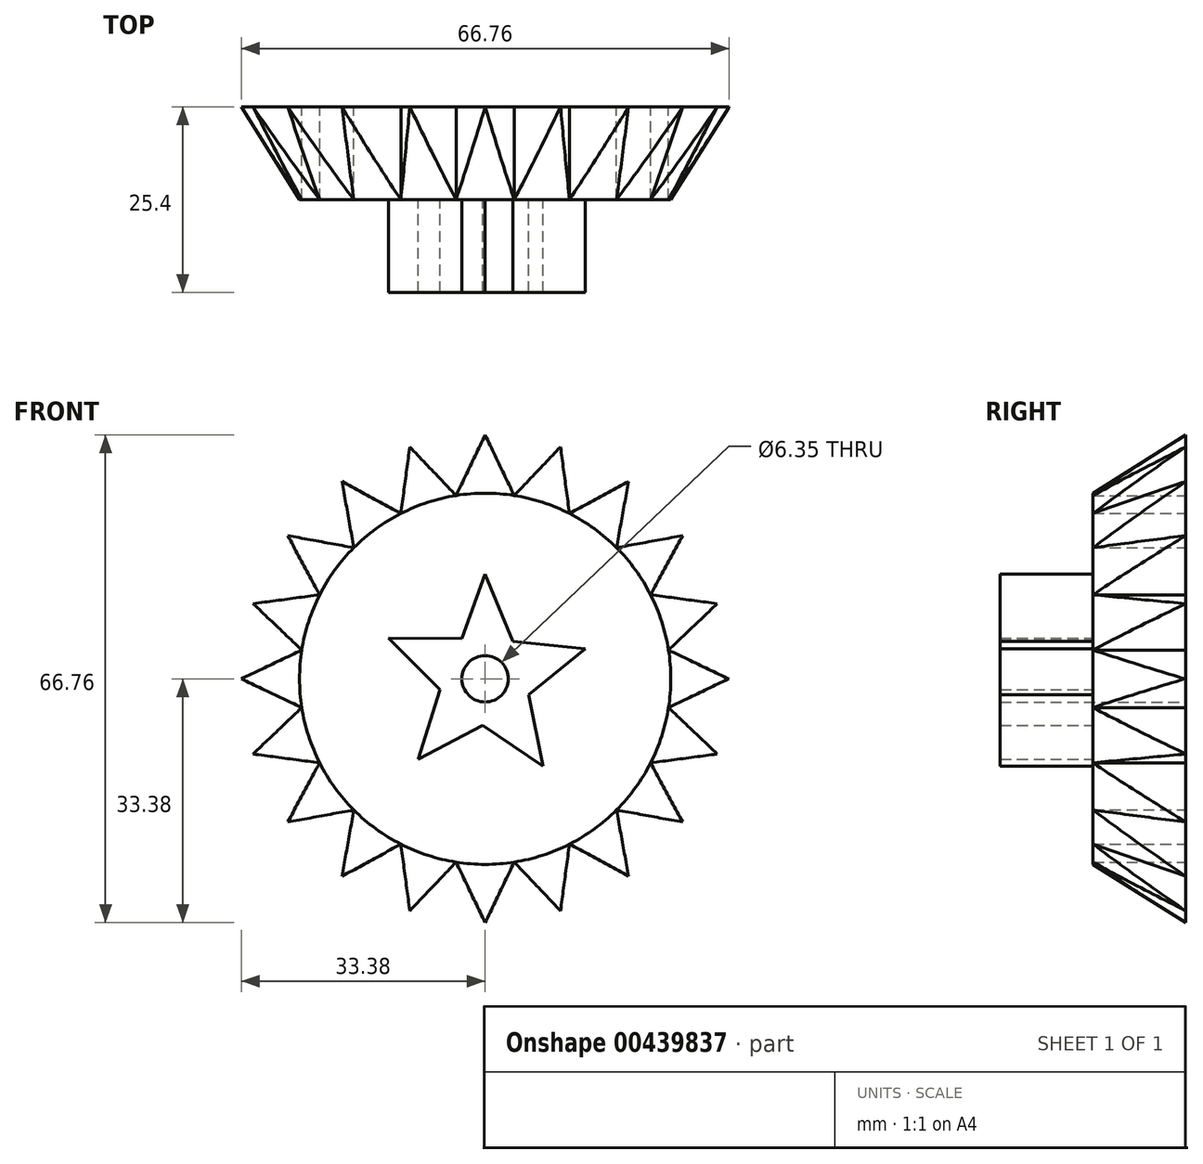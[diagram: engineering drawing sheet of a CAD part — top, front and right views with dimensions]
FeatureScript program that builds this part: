
annotation { "Feature Type Name" : "Feature", "Feature Type Description" : "" }
export const myFeature = defineFeature(function(context is Context, id is Id, definition is map)
    precondition{}
    {
        {
            var Q0;
            Q0=qCreatedBy(makeId("Front.planeOp"),FACE);
            var sketch = newSketch(context, id + "F0", { "sketchPlane" : qUnion([Q0])});
            skCircle(sketch, "E0", {"center": v(0, 0) * mm, "radius": 25.4 * mm});
            skPoint(sketch, "E1", {"position": v(0, 25.4) * mm});
            skPoint(sketch, "E2", {"position": v(3.98, 25.09) * mm});
            skPoint(sketch, "E3", {"position": v(7.86, 24.15) * mm});
            skPoint(sketch, "E4", {"position": v(11.54, 22.63) * mm});
            skPoint(sketch, "E5", {"position": v(14.94, 20.54) * mm});
            skPoint(sketch, "E6", {"position": v(17.98, 17.95) * mm});
            skPoint(sketch, "E7", {"position": v(20.56, 14.9) * mm});
            skPoint(sketch, "E8", {"position": v(22.64, 11.5) * mm});
            skPoint(sketch, "E9", {"position": v(24.17, 7.82) * mm});
            skPoint(sketch, "E10", {"position": v(25.1, 3.94) * mm});
            skPoint(sketch, "E11", {"position": v(25.4, -0.04) * mm});
            skPoint(sketch, "E12", {"position": v(25.08, -4.02) * mm});
            skPoint(sketch, "E13", {"position": v(24.14, -7.9) * mm});
            skPoint(sketch, "E14", {"position": v(22.6, -11.58) * mm});
            skPoint(sketch, "E15", {"position": v(20.52, -14.98) * mm});
            skPoint(sketch, "E16", {"position": v(17.92, -18) * mm});
            skPoint(sketch, "E17", {"position": v(14.88, -20.59) * mm});
            skPoint(sketch, "E18", {"position": v(11.47, -22.66) * mm});
            skPoint(sketch, "E19", {"position": v(7.78, -24.18) * mm});
            skPoint(sketch, "E20", {"position": v(3.9, -25.1) * mm});
            skPoint(sketch, "E21", {"position": v(-0.08, -25.4) * mm});
            skPoint(sketch, "E22.MirrorP", {"position": v(-3.98, 25.09) * mm});
            skPoint(sketch, "E23.MirrorP", {"position": v(-7.86, 24.15) * mm});
            skPoint(sketch, "E24.MirrorP", {"position": v(-11.54, 22.63) * mm});
            skPoint(sketch, "E25.MirrorP", {"position": v(-14.94, 20.54) * mm});
            skPoint(sketch, "E26.MirrorP", {"position": v(-17.98, 17.95) * mm});
            skPoint(sketch, "E27.MirrorP", {"position": v(-20.56, 14.9) * mm});
            skPoint(sketch, "E28.MirrorP", {"position": v(-22.64, 11.5) * mm});
            skPoint(sketch, "E29.MirrorP", {"position": v(-24.17, 7.82) * mm});
            skPoint(sketch, "E30.MirrorP", {"position": v(-25.1, 3.94) * mm});
            skPoint(sketch, "E31.MirrorP", {"position": v(-25.4, -0.04) * mm});
            skPoint(sketch, "E32.MirrorP", {"position": v(-25.08, -4.02) * mm});
            skPoint(sketch, "E33.MirrorP", {"position": v(-24.14, -7.9) * mm});
            skPoint(sketch, "E34.MirrorP", {"position": v(-22.6, -11.58) * mm});
            skPoint(sketch, "E35.MirrorP", {"position": v(-20.52, -14.98) * mm});
            skPoint(sketch, "E36.MirrorP", {"position": v(-17.92, -18) * mm});
            skPoint(sketch, "E37.MirrorP", {"position": v(-14.88, -20.59) * mm});
            skPoint(sketch, "E38.MirrorP", {"position": v(-11.47, -22.66) * mm});
            skPoint(sketch, "E39.MirrorP", {"position": v(-7.78, -24.18) * mm});
            skPoint(sketch, "E40.MirrorP", {"position": v(-3.9, -25.1) * mm});
            skLineSegment(sketch, "E41", {"start": v(0, 25.4) * mm, "end": v(-0.08, -25.4) * mm});
            skLineSegment(sketch, "E42", {"start": v(7.86, 24.15) * mm, "end": v(-7.78, -24.18) * mm});
            skLineSegment(sketch, "E43", {"start": v(14.94, 20.54) * mm, "end": v(-14.88, -20.59) * mm});
            skLineSegment(sketch, "E44", {"start": v(20.56, 14.9) * mm, "end": v(-20.52, -14.98) * mm});
            skLineSegment(sketch, "E45", {"start": v(24.17, 7.82) * mm, "end": v(-24.14, -7.9) * mm});
            skLineSegment(sketch, "E46", {"start": v(-25.4, -0.04) * mm, "end": v(25.4, -0.04) * mm});
            skLineSegment(sketch, "E47", {"start": v(24.14, -7.9) * mm, "end": v(-24.17, 7.82) * mm});
            skLineSegment(sketch, "E48", {"start": v(-20.56, 14.9) * mm, "end": v(20.52, -14.98) * mm});
            skLineSegment(sketch, "E49", {"start": v(14.88, -20.59) * mm, "end": v(-14.94, 20.54) * mm});
            skLineSegment(sketch, "E50", {"start": v(-7.86, 24.15) * mm, "end": v(7.78, -24.18) * mm});
            skLineSegment(sketch, "E51", {"start": v(0, 25.4) * mm, "end": v(0, 33.38) * mm});
            skLineSegment(sketch, "E52", {"start": v(0, 33.38) * mm, "end": v(3.98, 25.09) * mm});
            skLineSegment(sketch, "E53", {"start": v(7.86, 24.15) * mm, "end": v(10.31, 31.75) * mm});
            skLineSegment(sketch, "E54", {"start": v(-7.86, 24.15) * mm, "end": v(-10.31, 31.75) * mm});
            skLineSegment(sketch, "E55", {"start": v(-20.56, 14.9) * mm, "end": v(-27.02, 19.6) * mm});
            skLineSegment(sketch, "E56", {"start": v(-24.17, 7.82) * mm, "end": v(-31.76, 10.29) * mm});
            skLineSegment(sketch, "E57", {"start": v(14.94, 20.54) * mm, "end": v(19.63, 27) * mm});
            skLineSegment(sketch, "E58", {"start": v(20.56, 14.9) * mm, "end": v(27.02, 19.6) * mm});
            skLineSegment(sketch, "E59", {"start": v(24.17, 7.82) * mm, "end": v(31.76, 10.29) * mm});
            skLineSegment(sketch, "E60", {"start": v(25.4, -0.04) * mm, "end": v(33.38, -0.04) * mm});
            skLineSegment(sketch, "E61", {"start": v(-25.4, -0.04) * mm, "end": v(-33.38, 0) * mm});
            skLineSegment(sketch, "E62", {"start": v(-14.94, 20.54) * mm, "end": v(-19.6, 27.02) * mm});
            skLineSegment(sketch, "E63", {"start": v(0, 33.38) * mm, "end": v(-3.98, 25.09) * mm});
            skLineSegment(sketch, "E64", {"start": v(-3.98, 25.09) * mm, "end": v(-10.31, 31.75) * mm});
            skLineSegment(sketch, "E65", {"start": v(-10.31, 31.75) * mm, "end": v(-11.54, 22.63) * mm});
            skLineSegment(sketch, "E66", {"start": v(-11.54, 22.63) * mm, "end": v(-19.6, 27.02) * mm});
            skLineSegment(sketch, "E67", {"start": v(-19.6, 27.02) * mm, "end": v(-17.98, 17.95) * mm});
            skLineSegment(sketch, "E68", {"start": v(-17.98, 17.95) * mm, "end": v(-27.02, 19.6) * mm});
            skLineSegment(sketch, "E69", {"start": v(-27.02, 19.6) * mm, "end": v(-22.64, 11.5) * mm});
            skLineSegment(sketch, "E70", {"start": v(-22.64, 11.5) * mm, "end": v(-31.76, 10.29) * mm});
            skLineSegment(sketch, "E71", {"start": v(-31.76, 10.29) * mm, "end": v(-25.1, 3.94) * mm});
            skLineSegment(sketch, "E72", {"start": v(-25.1, 3.94) * mm, "end": v(-33.38, 0) * mm});
            skLineSegment(sketch, "E73", {"start": v(33.38, -0.04) * mm, "end": v(25.1, 3.94) * mm});
            skLineSegment(sketch, "E74", {"start": v(25.1, 3.94) * mm, "end": v(31.76, 10.29) * mm});
            skLineSegment(sketch, "E75", {"start": v(31.76, 10.29) * mm, "end": v(22.64, 11.5) * mm});
            skLineSegment(sketch, "E76", {"start": v(22.64, 11.5) * mm, "end": v(27.02, 19.6) * mm});
            skLineSegment(sketch, "E77", {"start": v(27.02, 19.6) * mm, "end": v(17.98, 17.95) * mm});
            skLineSegment(sketch, "E78", {"start": v(17.98, 17.95) * mm, "end": v(19.63, 27) * mm});
            skLineSegment(sketch, "E79", {"start": v(19.63, 27) * mm, "end": v(11.54, 22.63) * mm});
            skLineSegment(sketch, "E80", {"start": v(11.54, 22.63) * mm, "end": v(10.31, 31.75) * mm});
            skLineSegment(sketch, "E81", {"start": v(10.31, 31.75) * mm, "end": v(3.98, 25.09) * mm});
            skLineSegment(sketch, "E82.MirrorCS", {"start": v(-25.1, -3.94) * mm, "end": v(-33.38, 0) * mm});
            skLineSegment(sketch, "E83.MirrorCS", {"start": v(-31.76, -10.29) * mm, "end": v(-25.1, -3.94) * mm});
            skLineSegment(sketch, "E84.MirrorCS", {"start": v(-22.64, -11.5) * mm, "end": v(-31.76, -10.29) * mm});
            skLineSegment(sketch, "E85.MirrorCS", {"start": v(-27.02, -19.6) * mm, "end": v(-22.64, -11.5) * mm});
            skLineSegment(sketch, "E86.MirrorCS", {"start": v(-17.98, -17.95) * mm, "end": v(-27.02, -19.6) * mm});
            skLineSegment(sketch, "E87.MirrorCS", {"start": v(-19.6, -27.02) * mm, "end": v(-17.98, -17.95) * mm});
            skLineSegment(sketch, "E88.MirrorCS", {"start": v(-11.54, -22.63) * mm, "end": v(-19.6, -27.02) * mm});
            skLineSegment(sketch, "E89.MirrorCS", {"start": v(-10.31, -31.75) * mm, "end": v(-11.54, -22.63) * mm});
            skLineSegment(sketch, "E90.MirrorCS", {"start": v(-3.98, -25.09) * mm, "end": v(-10.31, -31.75) * mm});
            skLineSegment(sketch, "E91.MirrorCS", {"start": v(0, -33.38) * mm, "end": v(-3.98, -25.09) * mm});
            skLineSegment(sketch, "E92.MirrorCS", {"start": v(0, -33.38) * mm, "end": v(3.98, -25.09) * mm});
            skLineSegment(sketch, "E93.MirrorCS", {"start": v(10.31, -31.75) * mm, "end": v(3.98, -25.09) * mm});
            skLineSegment(sketch, "E94.MirrorCS", {"start": v(11.54, -22.63) * mm, "end": v(10.31, -31.75) * mm});
            skLineSegment(sketch, "E95.MirrorCS", {"start": v(19.63, -27) * mm, "end": v(11.54, -22.63) * mm});
            skLineSegment(sketch, "E96.MirrorCS", {"start": v(17.98, -17.95) * mm, "end": v(19.63, -27) * mm});
            skLineSegment(sketch, "E97.MirrorCS", {"start": v(27.02, -19.6) * mm, "end": v(17.98, -17.95) * mm});
            skLineSegment(sketch, "E98.MirrorCS", {"start": v(22.64, -11.5) * mm, "end": v(27.02, -19.6) * mm});
            skLineSegment(sketch, "E99.MirrorCS", {"start": v(31.76, -10.29) * mm, "end": v(22.64, -11.5) * mm});
            skLineSegment(sketch, "E100.MirrorCS", {"start": v(25.1, -3.94) * mm, "end": v(31.76, -10.29) * mm});
            skLineSegment(sketch, "E101.MirrorCS", {"start": v(33.38, 0.04) * mm, "end": v(25.1, -3.94) * mm});
            skSolve(sketch);
        }
        {
            var Q0;
            Q0 = qSketchRegion(id + "F0", true);
            extrude(context, id + "F1", {"entities" : qUnion([Q0]), "endBound" : BoundingType.SYMMETRIC, "depth" : 12.7 * mm});
        }
        {
            var Q0;
            Q0=qCreatedBy(makeId("Right.planeOp"),FACE);
            var sketch = newSketch(context, id + "F2", { "sketchPlane" : qUnion([Q0])});
            skLineSegment(sketch, "E102", {"start": v(0, 0) * mm, "end": v(-6.35, 0) * mm});
            skLineSegment(sketch, "E103", {"start": v(-6.35, 0) * mm, "end": v(-6.35, -25.4) * mm});
            skLineSegment(sketch, "E104", {"start": v(0, -33.38) * mm, "end": v(-6.35, -33.38) * mm});
            skLineSegment(sketch, "E105", {"start": v(-6.35, -33.38) * mm, "end": v(-6.35, -25.4) * mm});
            skLineSegment(sketch, "E106", {"start": v(0, -33.38) * mm, "end": v(6.35, -33.38) * mm});
            skLineSegment(sketch, "E107", {"start": v(6.35, -33.38) * mm, "end": v(-6.35, -25.4) * mm});
            skSolve(sketch);
        }
        {
            var Q0;
            Q0 = qSketchRegion(id + "F2", true);
            var Q1;
            Q1=sQuery(id+"F2.wireOp",EDGE,"E102");
            revolve(context, id + "F3", {"operationType" : NewBodyOperationType.REMOVE, "entities" : qUnion([Q0]), "axis" : qUnion([Q1]), "revolveType" : RevolveType.FULL, "oppositeDirection" : true});
        }
        {
            var Q0;
            Q0=makeQuery(id+"F1.opExtrude","CAP_FACE",FACE,{"disambiguationData":[OSD([sQuery(id+"F0.wireOp",EDGE,"E41"),sQuery(id+"F0.wireOp",EDGE,"E42"),sQuery(id+"F0.wireOp",EDGE,"E43"),sQuery(id+"F0.wireOp",EDGE,"E44"),sQuery(id+"F0.wireOp",EDGE,"E45"),sQuery(id+"F0.wireOp",EDGE,"E46"),sQuery(id+"F0.wireOp",EDGE,"E47"),sQuery(id+"F0.wireOp",EDGE,"E48"),sQuery(id+"F0.wireOp",EDGE,"E49"),sQuery(id+"F0.wireOp",EDGE,"E50"),sQuery(id+"F0.wireOp",EDGE,"E52"),sQuery(id+"F0.wireOp",EDGE,"E60"),sQuery(id+"F0.wireOp",EDGE,"E63"),sQuery(id+"F0.wireOp",EDGE,"E64"),sQuery(id+"F0.wireOp",EDGE,"E65"),sQuery(id+"F0.wireOp",EDGE,"E66"),sQuery(id+"F0.wireOp",EDGE,"E67"),sQuery(id+"F0.wireOp",EDGE,"E68"),sQuery(id+"F0.wireOp",EDGE,"E69"),sQuery(id+"F0.wireOp",EDGE,"E70"),sQuery(id+"F0.wireOp",EDGE,"E71"),sQuery(id+"F0.wireOp",EDGE,"E72"),sQuery(id+"F0.wireOp",EDGE,"E73"),sQuery(id+"F0.wireOp",EDGE,"E74"),sQuery(id+"F0.wireOp",EDGE,"E75"),sQuery(id+"F0.wireOp",EDGE,"E76"),sQuery(id+"F0.wireOp",EDGE,"E77"),sQuery(id+"F0.wireOp",EDGE,"E78"),sQuery(id+"F0.wireOp",EDGE,"E79"),sQuery(id+"F0.wireOp",EDGE,"E80"),sQuery(id+"F0.wireOp",EDGE,"E81"),sQuery(id+"F0.wireOp",EDGE,"E82.MirrorCS"),sQuery(id+"F0.wireOp",EDGE,"E83.MirrorCS"),sQuery(id+"F0.wireOp",EDGE,"E84.MirrorCS"),sQuery(id+"F0.wireOp",EDGE,"E85.MirrorCS"),sQuery(id+"F0.wireOp",EDGE,"E86.MirrorCS"),sQuery(id+"F0.wireOp",EDGE,"E87.MirrorCS"),sQuery(id+"F0.wireOp",EDGE,"E88.MirrorCS"),sQuery(id+"F0.wireOp",EDGE,"E89.MirrorCS"),sQuery(id+"F0.wireOp",EDGE,"E90.MirrorCS"),sQuery(id+"F0.wireOp",EDGE,"E91.MirrorCS"),sQuery(id+"F0.wireOp",EDGE,"E92.MirrorCS"),sQuery(id+"F0.wireOp",EDGE,"E93.MirrorCS"),sQuery(id+"F0.wireOp",EDGE,"E94.MirrorCS"),sQuery(id+"F0.wireOp",EDGE,"E95.MirrorCS"),sQuery(id+"F0.wireOp",EDGE,"E96.MirrorCS"),sQuery(id+"F0.wireOp",EDGE,"E97.MirrorCS"),sQuery(id+"F0.wireOp",EDGE,"E98.MirrorCS"),sQuery(id+"F0.wireOp",EDGE,"E99.MirrorCS"),sQuery(id+"F0.wireOp",EDGE,"E100.MirrorCS"),sQuery(id+"F0.wireOp",EDGE,"E101.MirrorCS")])],"isStart":false});
            var sketch = newSketch(context, id + "F4", { "sketchPlane" : qUnion([Q0])});
            skCircle(sketch, "E108", {"center": v(0, 0) * mm, "radius": 6.35 * mm});
            skPoint(sketch, "E109", {"position": v(0, 6.35) * mm});
            skPoint(sketch, "E110", {"position": v(3.79, 5.1) * mm});
            skPoint(sketch, "E111", {"position": v(6.08, 1.83) * mm});
            skPoint(sketch, "E112", {"position": v(5.97, -2.16) * mm});
            skPoint(sketch, "E113", {"position": v(3.5, -5.3) * mm});
            skPoint(sketch, "E114", {"position": v(-0.34, -6.34) * mm});
            skPoint(sketch, "E115", {"position": v(-4.06, -4.88) * mm});
            skPoint(sketch, "E116", {"position": v(-6.17, -1.5) * mm});
            skPoint(sketch, "E117", {"position": v(-5.85, 2.48) * mm});
            skPoint(sketch, "E118", {"position": v(-3.22, 5.48) * mm});
            skLineSegment(sketch, "E119", {"start": v(0, 6.35) * mm, "end": v(0, 0) * mm});
            skLineSegment(sketch, "E120", {"start": v(0, 0) * mm, "end": v(6.08, 1.83) * mm});
            skLineSegment(sketch, "E121", {"start": v(0, 0) * mm, "end": v(3.5, -5.3) * mm});
            skLineSegment(sketch, "E122", {"start": v(0, 0) * mm, "end": v(-4.06, -4.88) * mm});
            skLineSegment(sketch, "E123", {"start": v(0, 0) * mm, "end": v(-5.85, 2.48) * mm});
            skLineSegment(sketch, "E124", {"start": v(0, 6.35) * mm, "end": v(0, 14.33) * mm});
            skLineSegment(sketch, "E125", {"start": v(6.08, 1.83) * mm, "end": v(13.72, 4.13) * mm});
            skLineSegment(sketch, "E126", {"start": v(3.5, -5.3) * mm, "end": v(7.91, -11.95) * mm});
            skLineSegment(sketch, "E127", {"start": v(-4.06, -4.88) * mm, "end": v(-9.16, -11.02) * mm});
            skLineSegment(sketch, "E128", {"start": v(-5.85, 2.48) * mm, "end": v(-13.2, 5.6) * mm});
            skLineSegment(sketch, "E129", {"start": v(0, 14.33) * mm, "end": v(-3.22, 5.48) * mm});
            skLineSegment(sketch, "E130", {"start": v(-3.22, 5.48) * mm, "end": v(-13.2, 5.6) * mm});
            skLineSegment(sketch, "E131", {"start": v(-13.2, 5.6) * mm, "end": v(-6.17, -1.5) * mm});
            skLineSegment(sketch, "E132", {"start": v(-6.17, -1.5) * mm, "end": v(-9.16, -11.02) * mm});
            skLineSegment(sketch, "E133", {"start": v(-9.16, -11.02) * mm, "end": v(-0.34, -6.34) * mm});
            skLineSegment(sketch, "E134", {"start": v(-0.34, -6.34) * mm, "end": v(7.91, -11.95) * mm});
            skLineSegment(sketch, "E135", {"start": v(7.91, -11.95) * mm, "end": v(5.97, -2.16) * mm});
            skLineSegment(sketch, "E136", {"start": v(5.97, -2.16) * mm, "end": v(13.72, 4.13) * mm});
            skLineSegment(sketch, "E137", {"start": v(13.72, 4.13) * mm, "end": v(3.79, 5.1) * mm});
            skLineSegment(sketch, "E138", {"start": v(3.79, 5.1) * mm, "end": v(0, 14.33) * mm});
            skSolve(sketch);
        }
        {
            var Q0;
            Q0=qCreatedBy(makeId("Front.planeOp"),FACE);
            var sketch = newSketch(context, id + "F5", { "sketchPlane" : qUnion([Q0])});
            skCircle(sketch, "E139", {"center": v(0, 0) * mm, "radius": 3.17 * mm});
            skSolve(sketch);
        }
        {
            var Q0;
            Q0 = qSketchRegion(id + "F4", true);
            extrude(context, id + "F6", {"entities" : qUnion([Q0]), "operationType" : NewBodyOperationType.ADD, "depth" : 12.7 * mm});
        }
        {
            var Q0;
            Q0 = qSketchRegion(id + "F5", true);
            extrude(context, id + "F7", {"entities" : qUnion([Q0]), "operationType" : NewBodyOperationType.REMOVE, "endBound" : BoundingType.SYMMETRIC, "depth" : -127 * mm});
        }
    });
